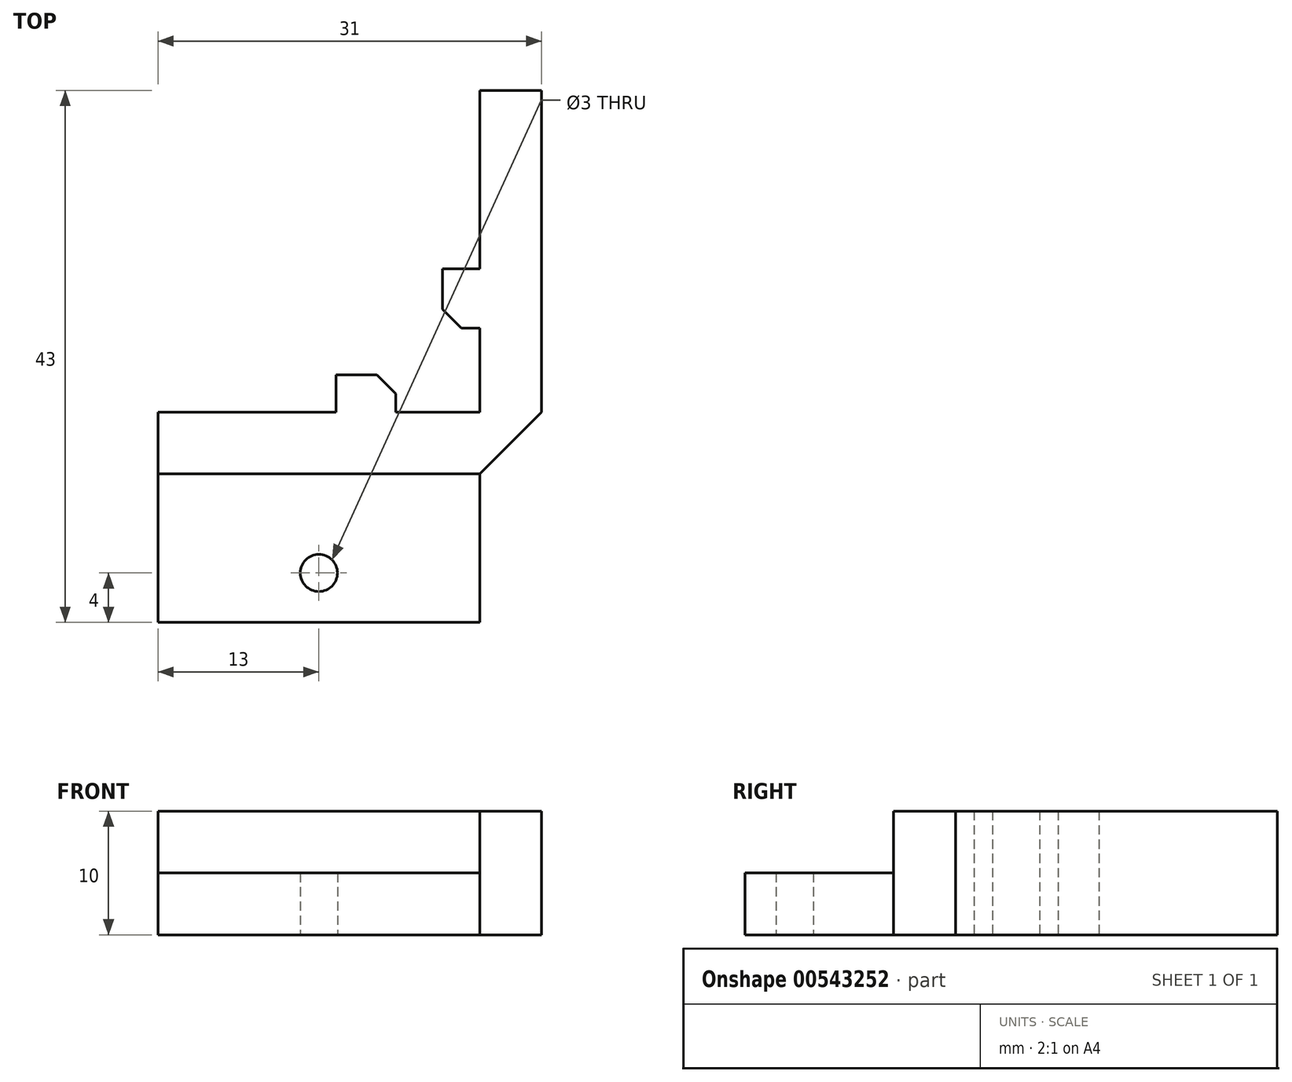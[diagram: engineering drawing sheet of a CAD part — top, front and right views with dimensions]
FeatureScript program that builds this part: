
annotation { "Feature Type Name" : "Feature", "Feature Type Description" : "" }
export const myFeature = defineFeature(function(context is Context, id is Id, definition is map)
    precondition{}
    {
        {
            var Q0;
            Q0=qCreatedBy(makeId("Top.planeOp"),FACE);
            var sketch = newSketch(context, id + "F0", { "sketchPlane" : qUnion([Q0])});
            skLineSegment(sketch, "E0.bottom", {"start": v(0, 0) * mm, "end": v(6, 0) * mm});
            skLineSegment(sketch, "E0.top", {"start": v(0, 20) * mm, "end": v(6, 20) * mm});
            skLineSegment(sketch, "E0.left", {"start": v(0, 0) * mm, "end": v(0, 6) * mm});
            skLineSegment(sketch, "E0.right", {"start": v(20, 0) * mm, "end": v(20, 6) * mm});
            skLineSegment(sketch, "E1.0", {"start": v(0, 14) * mm, "end": v(3, 14) * mm});
            skLineSegment(sketch, "E2.0", {"start": v(0, 6) * mm, "end": v(3, 6) * mm});
            skLineSegment(sketch, "E3.trimOffspring", {"start": v(0, 14) * mm, "end": v(0, 20) * mm});
            skLineSegment(sketch, "E4.trimOffspring", {"start": v(20, 14) * mm, "end": v(20, 20) * mm});
            skLineSegment(sketch, "E5.0", {"start": v(3, 6) * mm, "end": v(3, 14) * mm});
            skLineSegment(sketch, "E6.0", {"start": v(17, 6) * mm, "end": v(17, 14) * mm});
            skLineSegment(sketch, "E7.trimOffspring", {"start": v(17, 6) * mm, "end": v(20, 6) * mm});
            skLineSegment(sketch, "E8.trimOffspring", {"start": v(17, 14) * mm, "end": v(20, 14) * mm});
            skLineSegment(sketch, "E9.0", {"start": v(6, 0) * mm, "end": v(6, 3) * mm});
            skLineSegment(sketch, "E10.0", {"start": v(14, 0) * mm, "end": v(14, 3) * mm});
            skLineSegment(sketch, "E11.0", {"start": v(6, 3) * mm, "end": v(14, 3) * mm});
            skLineSegment(sketch, "E12.0", {"start": v(6, 17) * mm, "end": v(14, 17) * mm});
            skLineSegment(sketch, "E13.trimOffspring", {"start": v(14, 20) * mm, "end": v(20, 20) * mm});
            skLineSegment(sketch, "E14.trimOffspring", {"start": v(14, 0) * mm, "end": v(20, 0) * mm});
            skLineSegment(sketch, "E15.trimOffspring", {"start": v(6, 17) * mm, "end": v(6, 20) * mm});
            skLineSegment(sketch, "E16.trimOffspring", {"start": v(14, 17) * mm, "end": v(14, 20) * mm});
            skPoint(sketch, "E17.visualSharp", {"position": v(0, 20) * mm});
            skPoint(sketch, "E18.visualSharp", {"position": v(20, 20) * mm});
            skPoint(sketch, "E19.visualSharp", {"position": v(0, 0) * mm});
            skPoint(sketch, "E20.visualSharp", {"position": v(20, 0) * mm});
            skPoint(sketch, "E21.visualSharp", {"position": v(20, 6) * mm});
            skPoint(sketch, "E22.visualSharp", {"position": v(0, 6) * mm});
            skPoint(sketch, "E23.visualSharp", {"position": v(0, 14) * mm});
            skPoint(sketch, "E24.visualSharp", {"position": v(6, 20) * mm});
            skPoint(sketch, "E25.visualSharp", {"position": v(14, 20) * mm});
            skPoint(sketch, "E26.visualSharp", {"position": v(14, 0) * mm});
            skPoint(sketch, "E27.visualSharp", {"position": v(6, 0) * mm});
            skSolve(sketch);
        }
        {
            var Q0;
            Q0=qCreatedBy(makeId("Top.planeOp"),FACE);
            var sketch = newSketch(context, id + "F1", { "sketchPlane" : qUnion([Q0])});
            skLineSegment(sketch, "E28.0", {"start": v(20.9, 16.5) * mm, "end": v(20.9, 30.9) * mm});
            skLineSegment(sketch, "E28.1", {"start": v(17.9, 16.5) * mm, "end": v(20.9, 16.5) * mm});
            skLineSegment(sketch, "E28.2", {"start": v(17.9, 13.2) * mm, "end": v(17.9, 16.5) * mm});
            skLineSegment(sketch, "E28.3", {"start": v(20.9, 11.7) * mm, "end": v(19.4, 11.7) * mm});
            skLineSegment(sketch, "E28.4", {"start": v(20.9, 4.9) * mm, "end": v(20.9, 11.7) * mm});
            skLineSegment(sketch, "E28.6", {"start": v(14.1, 4.9) * mm, "end": v(20.9, 4.9) * mm});
            skLineSegment(sketch, "E28.7", {"start": v(14.1, 6.4) * mm, "end": v(14.1, 4.9) * mm});
            skLineSegment(sketch, "E28.8", {"start": v(9.3, 7.9) * mm, "end": v(12.6, 7.9) * mm});
            skLineSegment(sketch, "E28.9", {"start": v(9.3, 4.9) * mm, "end": v(9.3, 7.9) * mm});
            skLineSegment(sketch, "E28.19", {"start": v(-5.1, 4.9) * mm, "end": v(9.3, 4.9) * mm});
            skLineSegment(sketch, "E29.0", {"start": v(25.9, 4.9) * mm, "end": v(25.9, 30.9) * mm});
            skLineSegment(sketch, "E30", {"start": v(-5.1, -0.1) * mm, "end": v(-5.1, 4.9) * mm});
            skLineSegment(sketch, "E31", {"start": v(25.9, 30.9) * mm, "end": v(20.9, 30.9) * mm});
            skLineSegment(sketch, "E32", {"start": v(25.9, 4.9) * mm, "end": v(20.9, -0.1) * mm});
            skLineSegment(sketch, "E33", {"start": v(19.4, 11.7) * mm, "end": v(17.9, 13.2) * mm});
            skLineSegment(sketch, "E34", {"start": v(14.1, 6.4) * mm, "end": v(12.6, 7.9) * mm});
            skLineSegment(sketch, "E35", {"start": v(20.9, -0.1) * mm, "end": v(20.9, -12.1) * mm});
            skLineSegment(sketch, "E36", {"start": v(20.9, -12.1) * mm, "end": v(-5.1, -12.1) * mm});
            skLineSegment(sketch, "E37", {"start": v(-5.1, -12.1) * mm, "end": v(-5.1, -0.1) * mm});
            skPoint(sketch, "E38", {"position": v(7.9, -8.1) * mm});
            skPoint(sketch, "E38.positionSnap0", {"position": v(20.9, -6.1) * mm});
            skPoint(sketch, "E38.positionSnap1", {"position": v(7.9, -12.1) * mm});
            skLineSegment(sketch, "E39", {"start": v(-5.1, -0.1) * mm, "end": v(20.9, -0.1) * mm});
            skSolve(sketch);
        }
        {
            var Q0;
            Q0=makeQuery(id+"F1.imprint","IMPRINT",FACE,{"disambiguationData":[TD([[makeQuery(id+"F1.imprint","IMPRINT",EDGE,{"derivedFrom":sQuery(id+"F1.wireOp",EDGE,"E28.0")}),-1.0]])]});
            extrude(context, id + "F2", {"entities" : qUnion([Q0]), "depth" : 10 * mm, "offsetDistance" : 25 * mm});
        }
        {
            var Q0;
            Q0=makeQuery(id+"F1.imprint","IMPRINT",FACE,{"disambiguationData":[TD([[makeQuery(id+"F1.imprint","IMPRINT",EDGE,{"derivedFrom":sQuery(id+"F1.wireOp",EDGE,"E35")}),-1.0]])]});
            extrude(context, id + "F3", {"entities" : qUnion([Q0]), "operationType" : NewBodyOperationType.ADD, "depth" : 5 * mm, "offsetDistance" : 25 * mm});
        }
        {
            var Q0;
            Q0=sQuery(id+"F1.wireOp",VERTEX,"E38");
            var Q1;
            Q1=makeQuery(id+"F2.opExtrude","SWEPT_BODY",BODY,{"disambiguationData":[OSD([sQuery(id+"F1.wireOp",EDGE,"E28.0"),sQuery(id+"F1.wireOp",EDGE,"E28.1"),sQuery(id+"F1.wireOp",EDGE,"E28.2"),sQuery(id+"F1.wireOp",EDGE,"E28.3"),sQuery(id+"F1.wireOp",EDGE,"E28.4"),sQuery(id+"F1.wireOp",EDGE,"E28.6"),sQuery(id+"F1.wireOp",EDGE,"E28.7"),sQuery(id+"F1.wireOp",EDGE,"E28.8"),sQuery(id+"F1.wireOp",EDGE,"E28.9"),sQuery(id+"F1.wireOp",EDGE,"E28.19"),sQuery(id+"F1.wireOp",EDGE,"E29.0"),sQuery(id+"F1.wireOp",EDGE,"E30"),sQuery(id+"F1.wireOp",EDGE,"E31"),sQuery(id+"F1.wireOp",EDGE,"E32"),sQuery(id+"F1.wireOp",EDGE,"E33"),sQuery(id+"F1.wireOp",EDGE,"E34"),sQuery(id+"F1.wireOp",EDGE,"E39")])]});
            hole(context, id + "F4", {"style" : HoleStyle.SIMPLE, "endStyle" : HoleEndStyle.THROUGH, "oppositeDirection" : true, "holeDiameter" : 3 * mm, "isTappedThrough" : true, "tappedDepth" : 12 * mm, "tapClearance" : 3, "locations" : qUnion([Q0]), "scope" : qUnion([Q1])});
        }
    });
